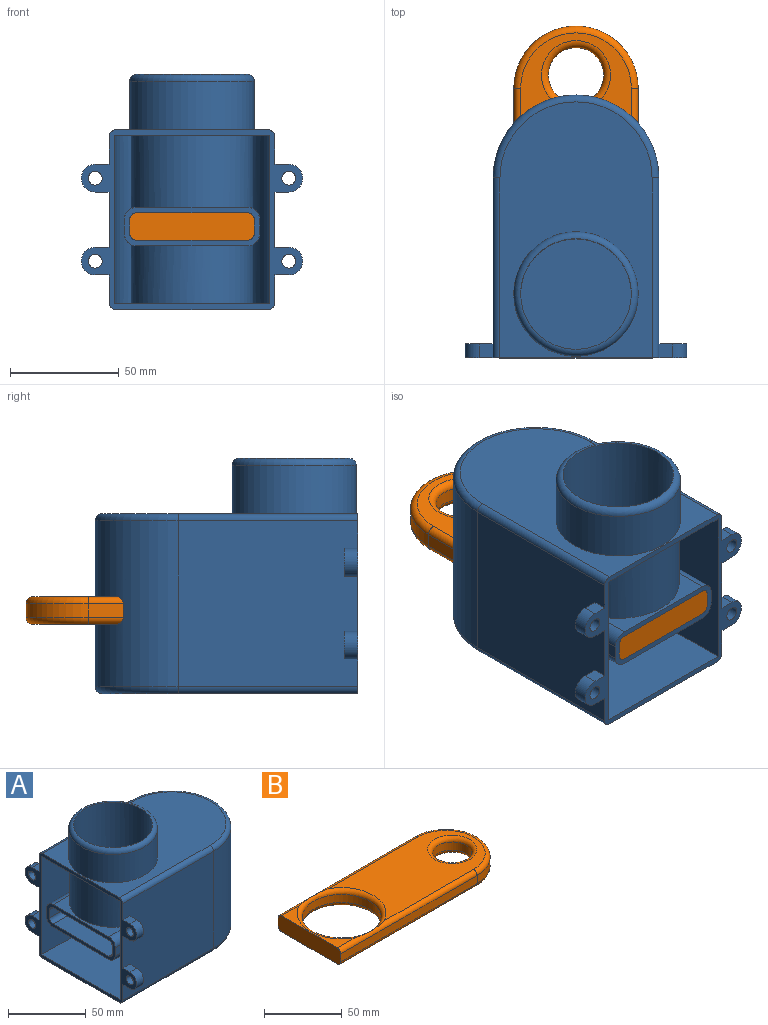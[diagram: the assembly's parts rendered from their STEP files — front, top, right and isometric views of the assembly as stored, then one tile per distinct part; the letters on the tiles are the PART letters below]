
ASSEMBLY  parts=2 mates=1
PART A: 64 faces, bbox 125.5x101.6x108 mm
  f0: plane 101.6x82.55mm, normal (-1,0,0), area 1221.2mm2, adj f1,f4,f8,f18,f20,f21,f25,f35
  f1: plane 82.55x76.2mm, normal (0,-1,0), area 6129mm2, adj f0,f3,f39,f40,f41,f45,f46,f47
  f2: plane 62.23x17.78mm, normal (-1,0,0), area 361.3mm2, adj f7,f10,f11,f12,f14,f15,f16,f17
  f3: cylinder r=38.1mm len=76.2mm, axis (0,0,-1), area 8312.7mm2, adj f1,f4,f6,f9,f10,f12,f14,f15
  f4: plane 82.55x76.2mm, normal (0,1,0), area 6129mm2, adj f0,f3,f36,f37,f38,f42,f43,f44
  f5: cylinder r=25.4mm len=63.5mm, axis (0,0,1), area 10134.1mm2, adj f7,f9,f63
  f6: plane 50.8x38.1mm, normal (0,0,1), area 767.2mm2, adj f3,f13,f15,f16
  f7: plane 50.8x29.21mm, normal (0,0,-1), area 470.5mm2, adj f2,f5,f14,f17
  f8: plane 117.48x69.85mm, normal (0,0,-1), area 5655.3mm2, adj f0,f13,f60,f61,f62
  f9: plane 91.44x50.8mm, normal (0,0,-1), area 3476.8mm2, adj f3,f5,f14,f17
  f10: plane 107.75x6.35mm, normal (0,-1,0), area 684.2mm2, adj f2,f3,f14,f15
  f11: plane 82.55x50.8mm, normal (0,0,1), area 3180.1mm2, adj f2,f13,f15,f16
  f12: plane 107.75x6.35mm, normal (0,1,0), area 684.2mm2, adj f2,f3,f16,f17
  f13: cylinder r=25.4mm len=50.8mm, axis (0,0,-1), area 5067.1mm2, adj f6,f8,f11
  f14: cylinder r=3.17mm len=110.95mm, axis (-1,0,0), area 543.4mm2, adj f2,f3,f7,f9,f10
  f15: cylinder r=3.17mm len=110.95mm, axis (1,0,0), area 543.4mm2, adj f2,f3,f6,f10,f11
  f16: cylinder r=3.17mm len=110.95mm, axis (-1,0,0), area 543.4mm2, adj f2,f3,f6,f11,f12
  f17: cylinder r=3.17mm len=110.95mm, axis (1,0,0), area 543.4mm2, adj f2,f3,f7,f9,f12
  f18: plane 117.48x69.85mm, normal (0,0,1), area 5116.9mm2, adj f0,f56,f57,f58,f59
  f19: cylinder r=35.56mm len=77.47mm, axis (0,0,-1), area 7359.4mm2, adj f20,f21,f23,f25,f26,f27,f29,f31
  f20: plane 82.55x77.47mm, normal (0,-1,0), area 6395.1mm2, adj f0,f19,f25,f35
  f21: plane 82.55x77.47mm, normal (0,1,0), area 6395.1mm2, adj f0,f19,f25,f35
  f22: cylinder r=27.94mm len=55.88mm, axis (0,0,1), area 5811.7mm2, adj f24,f26,f31,f34,f35
  f23: plane 50.8x23.92mm, normal (0,0,-1), area 451.7mm2, adj f19,f30,f32,f33
  f24: plane 50.8x17.57mm, normal (0,0,1), area 297.4mm2, adj f2,f22,f31,f34
  f25: plane 118.11x71.12mm, normal (0,0,1), area 5404.8mm2, adj f0,f19,f20,f21,f30
  f26: plane 77.26x50.8mm, normal (0,0,1), area 3161.4mm2, adj f19,f22,f31,f34
  f27: plane 99.77x6.35mm, normal (0,1,0), area 633.5mm2, adj f2,f19,f31,f32
  f28: plane 70.91x50.8mm, normal (0,0,-1), area 3007.1mm2, adj f2,f30,f32,f33
  f29: plane 99.77x6.35mm, normal (0,-1,0), area 633.5mm2, adj f2,f19,f33,f34
  f30: cylinder r=27.94mm len=55.88mm, axis (0,0,-1), area 4697mm2, adj f23,f25,f28,f32,f33
  f31: cylinder r=5.71mm len=107.44mm, axis (-1,0,0), area 882.6mm2, adj f2,f19,f22,f24,f26,f27
  f32: cylinder r=5.71mm len=107.44mm, axis (1,0,0), area 882.6mm2, adj f2,f19,f23,f27,f28,f30
  f33: cylinder r=5.71mm len=107.44mm, axis (-1,0,0), area 882.6mm2, adj f2,f19,f23,f28,f29,f30
  f34: cylinder r=5.71mm len=107.44mm, axis (1,0,0), area 882.6mm2, adj f2,f19,f22,f24,f26,f29
  f35: plane 118.11x71.12mm, normal (0,0,-1), area 5404.8mm2, adj f0,f19,f20,f21,f22
  f36: plane 6.35x6.35mm, normal (0,0,-1), area 40.3mm2, adj f0,f4,f38,f55
  f37: plane 6.35x6.35mm, normal (0,0,1), area 40.3mm2, adj f0,f4,f38,f55
  f38: plane 12.7x12.7mm, normal (1,0,0), area 112.3mm2, adj f4,f36,f37,f51,f55
  f39: plane 6.35x6.35mm, normal (0,0,1), area 40.3mm2, adj f0,f1,f41,f53
  f40: plane 6.35x6.35mm, normal (0,0,-1), area 40.3mm2, adj f0,f1,f41,f53
  f41: plane 12.7x12.7mm, normal (1,0,0), area 112.3mm2, adj f1,f39,f40,f50,f53
  f42: plane 6.35x6.35mm, normal (0,0,1), area 40.3mm2, adj f0,f4,f44,f54
  f43: plane 6.35x6.35mm, normal (0,0,-1), area 40.3mm2, adj f0,f4,f44,f54
  f44: plane 12.7x12.7mm, normal (1,0,0), area 112.3mm2, adj f4,f42,f43,f49,f54
  f45: plane 6.35x6.35mm, normal (0,0,-1), area 40.3mm2, adj f0,f1,f47,f52
  f46: plane 6.35x6.35mm, normal (0,0,1), area 40.3mm2, adj f0,f1,f47,f52
  f47: plane 12.7x12.7mm, normal (1,0,0), area 112.3mm2, adj f1,f45,f46,f48,f52
  f48: cylinder r=3.17mm len=6.35mm, axis (-1,0,0), area 126.7mm2, adj f0,f47
  f49: cylinder r=3.17mm len=6.35mm, axis (-1,0,0), area 126.7mm2, adj f0,f44
  f50: cylinder r=3.17mm len=6.35mm, axis (-1,0,0), area 126.7mm2, adj f0,f41
  f51: cylinder r=3.17mm len=6.35mm, axis (-1,0,0), area 126.7mm2, adj f0,f38
  f52: cylinder r=6.35mm len=12.7mm, axis (1,0,0), area 126.7mm2, adj f0,f45,f46,f47
  f53: cylinder r=6.35mm len=12.7mm, axis (-1,0,0), area 126.7mm2, adj f0,f39,f40,f41
  f54: cylinder r=6.35mm len=12.7mm, axis (1,0,0), area 126.7mm2, adj f0,f42,f43,f44
  f55: cylinder r=6.35mm len=12.7mm, axis (1,0,0), area 126.7mm2, adj f0,f36,f37,f38
  f56: cylinder r=28.57mm len=57.15mm, axis (0,0,-1), area 3990.3mm2, adj f18,f63
  f57: cylinder r=3.17mm len=82.55mm, axis (-1,0,0), area 411.7mm2, adj f0,f1,f18,f58
  f58: torus R=34.92mm, axis (0,0,1), area 578.9mm2, adj f3,f18,f57,f59
  f59: cylinder r=3.17mm len=82.55mm, axis (1,0,0), area 411.7mm2, adj f0,f4,f18,f58
  f60: cylinder r=3.17mm len=82.55mm, axis (1,0,0), area 411.7mm2, adj f0,f1,f8,f61
  f61: torus R=34.92mm, axis (0,0,1), area 578.9mm2, adj f3,f8,f60,f62
  f62: cylinder r=3.17mm len=82.55mm, axis (-1,0,0), area 411.7mm2, adj f0,f4,f8,f61
  f63: torus R=25.4mm, axis (0,0,1), area 859.3mm2, adj f5,f56
PART B: 20 faces, bbox 158.9x66.7x12.7 mm
  f0: plane 106.92x50.8mm, normal (0,0,1), area 3801.6mm2, adj f14,f15,f16,f17,f19
  f1: plane 106.92x50.8mm, normal (0,0,-1), area 3801.6mm2, adj f10,f11,f12,f13,f18
  f2: plane 50.8x16.12mm, normal (0,0,1), area 257.3mm2, adj f6,f14,f15,f17
  f3: plane 50.8x16.12mm, normal (0,0,-1), area 257.3mm2, adj f6,f10,f11,f13
  f4: plane 123.83x6.35mm, normal (0,-1,0), area 786.3mm2, adj f6,f8,f10,f17
  f5: plane 123.83x6.35mm, normal (0,1,0), area 786.3mm2, adj f6,f8,f13,f14
  f6: plane 57.15x12.7mm, normal (-1,0,0), area 717.2mm2, adj f2,f3,f4,f5,f10,f13,f14,f17
  f7: cylinder r=25.4mm len=50.8mm, axis (0,0,1), area 1013.4mm2, adj f11,f15
  f8: cylinder r=28.57mm len=57.15mm, axis (0,0,1), area 570mm2, adj f4,f5,f12,f16
  f9: cylinder r=12.7mm len=25.4mm, axis (0,0,1), area 506.7mm2, adj f18,f19
  f10: cylinder r=3.17mm len=123.83mm, axis (-1,0,0), area 589mm2, adj f1,f3,f4,f6,f11,f12
  f11: torus R=28.57mm, axis (0,0,1), area 773.6mm2, adj f1,f3,f7,f10,f13
  f12: torus R=25.4mm, axis (0,0,1), area 429.6mm2, adj f1,f8,f10,f13
  f13: cylinder r=3.17mm len=123.83mm, axis (1,0,0), area 589mm2, adj f1,f3,f5,f6,f11,f12
  f14: cylinder r=3.17mm len=123.83mm, axis (-1,0,0), area 589mm2, adj f0,f2,f5,f6,f15,f16
  f15: torus R=28.57mm, axis (0,0,1), area 773.6mm2, adj f0,f2,f7,f14,f17
  f16: torus R=25.4mm, axis (0,0,1), area 429.6mm2, adj f0,f8,f14,f17
  f17: cylinder r=3.17mm len=123.83mm, axis (1,0,0), area 589mm2, adj f0,f2,f4,f6,f15,f16
  f18: torus R=15.88mm, axis (0,0,1), area 434.1mm2, adj f1,f9
  f19: torus R=15.88mm, axis (0,0,1), area 434.1mm2, adj f0,f9
PLACE A rot(axis=(0,0,1),90deg) t=(-35.56,82.55,-2.54)mm
PLACE B rot(axis=(0,0,1),90deg) t=(-35.56,0,35.56)mm
MATE slider B.f6 <-> A.f2  axis (0,-1,0) through (-35.56,0,35.56)mm
